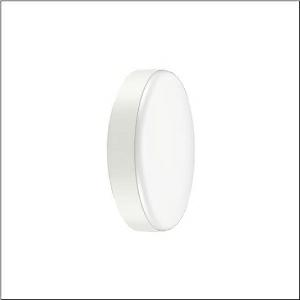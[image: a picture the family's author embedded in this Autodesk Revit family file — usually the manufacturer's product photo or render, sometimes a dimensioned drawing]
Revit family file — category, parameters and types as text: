
# Revit family: round_31_51wc10db44a
name_source: partatom
category: Lighting Fixtures
units: mm (PartAtom-declared; Revit-internal decimal feet)

## family parameters
Cut with Voids When Loaded = No
Host = Face
Light Source = No
Part Type = Normal
Room Calculation Point = No
Round Connector Dimension = Use Diameter
Shared = No

## types (1)
- Round 31 (1 x LED, 4400 lm, 34 W, 4000K)
    Apparent Load = 34 VA
    CIE Flux Codes = 44 75 94 94 100
    Color Rendering = 80
    Color Temperature = 4000K
    Default Elevation = 1800 mm
    Description = Round 31, wall and ceiling luminaire, primary optical cover: cover, of PC, opal, light emission: direct distribution, primary light characteristic: symmetric, installation type: surface-mounted, LED, rated luminous flux: 4.400lm, luminous efficacy: 129lm/W, light colour: 840, colour temperature: 4000K, control gear: DALI 2, with terminal, 3-pole, max. 2.5mm², mains connection: 220..240V, AC, 50/60Hz, rated input power: 34W, luminaire housing, of PC, traffic white (RAL 9016), diameter: 480mm, protection rating (complete): IP65, insulation class (complete): insulation class II (safety insulation), certification: CE, impact resistance: IK10, permissible operating ambient temperature: -20..+40°C, permissible storage temperature: -20..+60°C, packaging unit: 1 piece
    Height = 97 mm
    Lamp = 1 x LED
    Lamp Light Flux = 4400 lm
    Lamp Power = 34 W
    Lamp count = 1
    Length = 480 mm
    Luminous efficacy = 129 lm/W
    Manufacturer = Siteco
    ModVariant = No
    Model = 51WC10DB44A
    Mounting Place = Ceiling
    Mounting Type = Surface mounted
    Number of Poles = 1
    OnlyDefault = Yes
    Power Factor = 1
    Product Name = Round 31
    Product group = wall and ceiling luminaire | ceiling mounted
    ProductGroupID = 305
    Protection Class = Protection class II
    Protection Degree = IP 65
    RLX_Detail_Level = 1
    RLX_Emergency_Light_Flux = 0 lm
    RLX_Emergency_Type = 0
    RLX_Emergency_Type_DB = No
    RlxData = <blob elided: 41741 chars, md5=74767e30>
    Socket = socket
    Standby Power = 0 W
    System Light Flux = 4400 lm
    System Power = 34 W
    Type Comments = Product without accessories
    Type Image = l_1007188.jpg
    URL = http://relux.com
    VarID = ---
    Voltage = 0 V
    Weight = 0.00 kg
    Width = 0 mm  [stored 0 ft]

note: [stored X ft] marks values corroborated as IEEE doubles in the binary element streams (Revit-internal decimal feet)

## geometry (parser evidence)
native form markers: Blend x4, Sweep x13
no freeform markers — native parametric forms only
